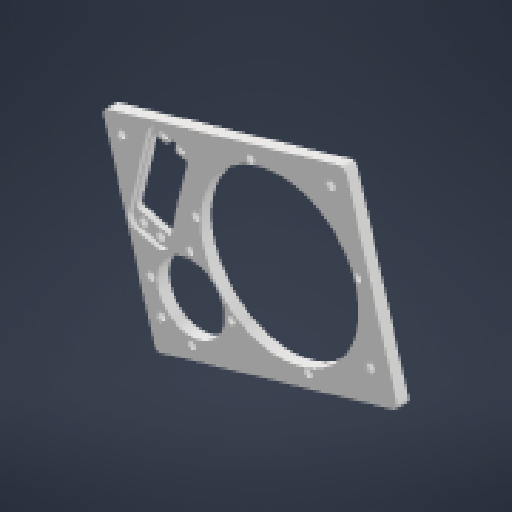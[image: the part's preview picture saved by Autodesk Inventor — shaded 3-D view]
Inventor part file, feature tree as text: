
AUTODESK INVENTOR PART (.ipt)
format: ipt  version: 2024.2 (Build 282272000, 272)  size: 320,512 bytes
history: native  units: in
note: dims shown in document units (in); Inventor stores cm internally (conversion verified against a paired STEP export)
features: reference x20, other x8, extrude x5, sketch x5, fillet x2
ambient origin geometry x8: Origin, YZ Plane, XZ Plane, XY Plane, X Axis, Y Axis, Z Axis, Center Point
bodies: Solid1 (feature_tree)
feature tree (40):
  extrude  "Extrusion1"  Depth=0.1693in
  extrude  "Extrusion2"  Depth=0.1693in
  extrude  "Extrusion3"  TaperAngle=0.0deg  [1 undecoded]
  fillet  "Fillet1"  Radius=0.1969in
  fillet  "Fillet2"  Radius=0.1969in
  extrude  "Extrusion4"  Depth=0.1969in
  extrude  "Extrusion5"  Depth=0.25in TaperAngle=0.0deg
  sketch  "Sketch1"  dims[d4=0.1693in d5=0.1693in]
  reference  "Reference1"
  reference  "Reference2"
  reference  "Reference4"
  reference  "Reference9"
  reference  "Reference10"
  reference  "Reference11"
  reference  "Reference12"
  reference  "Reference13"
  reference  "Reference14"
  sketch  "Sketch3"  dims[d6=0.1693in d7=0.1693in]
  sketch  "Sketch4"  dims[d8=0.1969in d10=0.0in d11=0.1969in d12=0.1969in]
  reference  "Reference15"
  reference  "Reference16"
  reference  "Reference17"
  sketch  "Sketch5"  dims[d13=0.0in d14=0.1969in]
  reference  "Reference18"
  reference  "Reference19"
  reference  "Reference20"
  reference  "Reference21"
  sketch  "Sketch6"  dims[d15=0.1969in d16=0.25in d17=0.0in d18=0.2697in d19=0.0in d20=0.0in d21=0.1073in d22=0.0in d23=0.05in d24=0.05in d25=0.3787in d26=0.8453in d27=0.3197in d28=0.2in d29=0.1693in d30=0.1693in d31=0.1693in d32=0.1693in d33=0.2362in d34=0.2362in d35=0.05in d36=0.0in d37=0.0in d38=0.0in d39=0.025in d40=0.0625in d41=0.025in d42=0.125in d43=0.2402in d44=0.2402in d45=0.2402in d46=0.2402in d47=0.0059in d48=0.0in d49=0.0in d50=0.0in]
  reference  "Reference22"
  reference  "Reference23"
  reference  "Reference24"
  reference  "Reference25"
  other  "<userpath>\Desktop\Robotics\Swerve2\Assemblies\Pod.iam"
  other  "Pod.iam"
  other  "big_funny_washer:1"
  other  "5000-0002-0001 assembly_1"
  other  "5000-0002-0001 motor shield_13"
  other  "Axon_MINI:1"
  parser-record x1  (decoder bookkeeping rows leaked as tree rows — omitted from the tree; the rows remain in map.json)
  other  "Upper_Plate:1"
note: 1 required parameter value undecoded (feature->parameter linkage not recoverable at this tier; creation-order binding heuristic only, values carry confidence <= 0.55)
